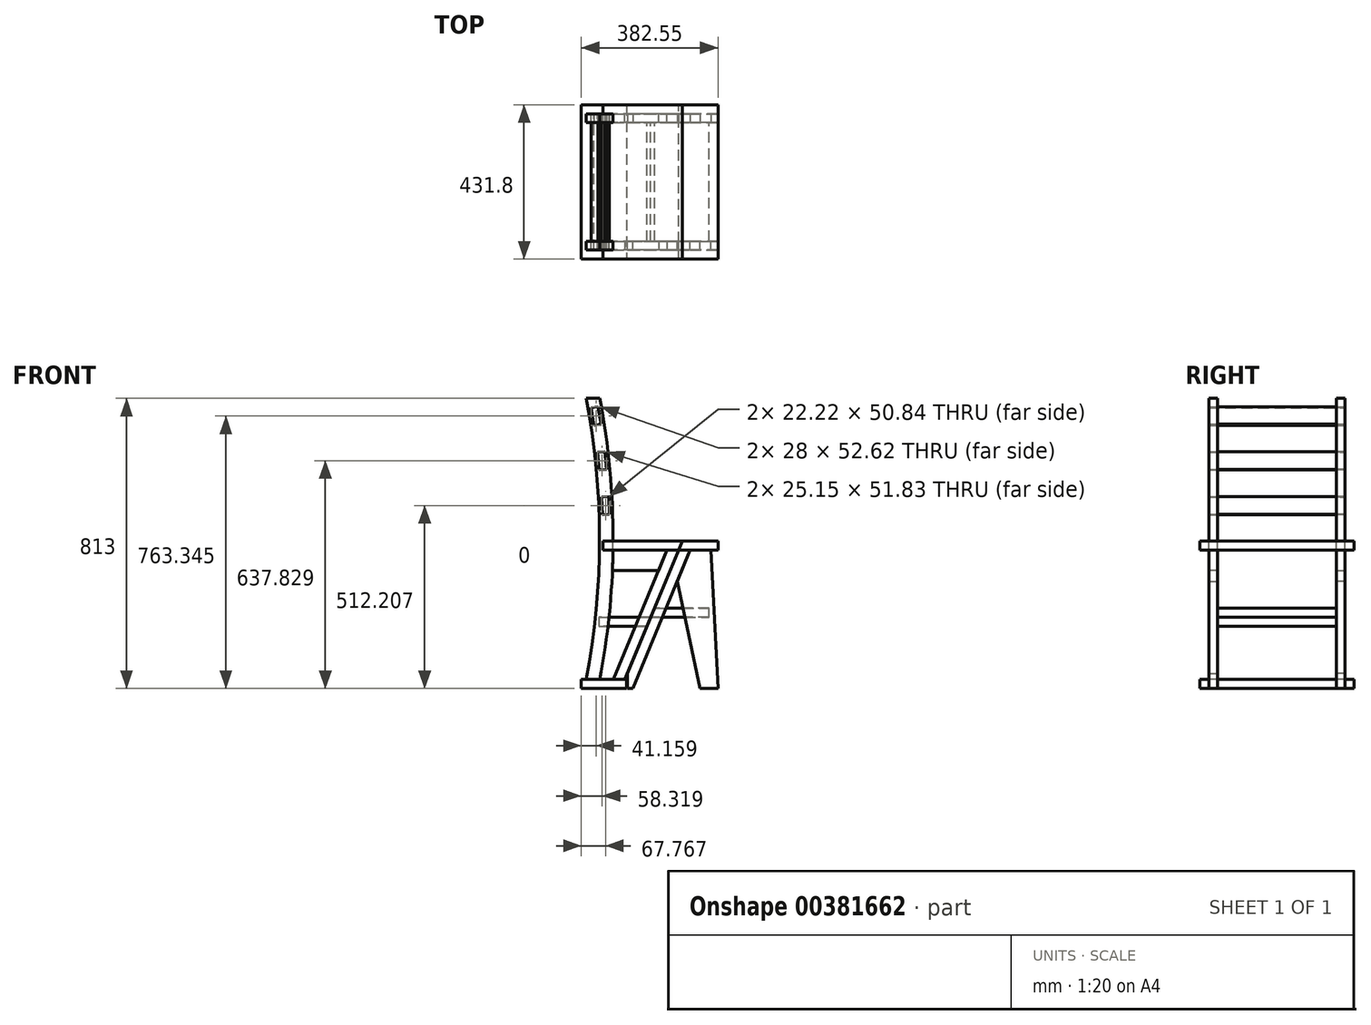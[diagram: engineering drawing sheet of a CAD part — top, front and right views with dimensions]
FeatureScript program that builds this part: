
annotation { "Feature Type Name" : "Feature", "Feature Type Description" : "" }
export const myFeature = defineFeature(function(context is Context, id is Id, definition is map)
    precondition{}
    {
        {
            var Q0;
            Q0=qCreatedBy(makeId("Front.planeOp"),FACE);
            var sketch = newSketch(context, id + "F0", { "sketchPlane" : qUnion([Q0])});
            skLineSegment(sketch, "E0.bottom", {"start": v(0, 25.4) * mm, "end": v(127, 25.4) * mm});
            skLineSegment(sketch, "E0.top", {"start": v(0, 0) * mm, "end": v(127, 0) * mm});
            skLineSegment(sketch, "E0.left", {"start": v(0, 25.4) * mm, "end": v(0, 0) * mm});
            skLineSegment(sketch, "E0.right", {"start": v(127, 25.4) * mm, "end": v(127, 0) * mm});
            skSolve(sketch);
        }
        {
            var Q0;
            Q0 = qSketchRegion(id + "F0", true);
            extrude(context, id + "F1", {"entities" : qUnion([Q0]), "oppositeDirection" : true, "depth" : 431.8 * mm, "offsetDistance" : 25.4 * mm});
        }
        {
            var Q0;
            Q0=makeQuery(id+"F1.opExtrude","SWEPT_EDGE",EDGE,{"disambiguationData":[OSD([sQuery(id+"F0.wireOp",EDGE,"E0.bottom"),sQuery(id+"F0.wireOp",EDGE,"E0.right")])]});
            cPoint(context, id + "F2", {"entities" : qUnion([Q0]), "parameter" : 0.5});
        }
        {
            var Q0;
            Q0=qCreatedBy(makeId("Front.planeOp"),FACE);
            var Q1;
            Q1 = qCreatedBy(id + "F2" ,VERTEX);
            cPlane(context, id + "F3", {"entities" : qUnion([Q0, Q1]), "cplaneType" : CPlaneType.PLANE_POINT, "offset" : 25 * mm, "width" : 150 * mm, "height" : 150 * mm});
        }
        {
            var Q0;
            Q0=makeQuery(id+"F1.opExtrude","CAP_FACE",FACE,{"disambiguationData":[OSD([sQuery(id+"F0.wireOp",EDGE,"E0.bottom"),sQuery(id+"F0.wireOp",EDGE,"E0.top"),sQuery(id+"F0.wireOp",EDGE,"E0.left"),sQuery(id+"F0.wireOp",EDGE,"E0.right")])],"isStart":true});
            cPlane(context, id + "F4", {"entities" : qUnion([Q0]), "cplaneType" : CPlaneType.OFFSET, "offset" : 25 * mm, "oppositeDirection" : true, "width" : 150 * mm, "height" : 150 * mm});
        }
        {
            var Q0;
            Q0=qCreatedBy(id+"F4.planeOp",FACE);
            cPlane(context, id + "F5", {"entities" : qUnion([Q0]), "cplaneType" : CPlaneType.OFFSET, "offset" : 25 * mm, "oppositeDirection" : true, "width" : 150 * mm, "height" : 150 * mm});
        }
        {
            var Q0;
            Q0=qCreatedBy(id+"F3.planeOp",FACE);
            var sketch = newSketch(context, id + "F6", { "sketchPlane" : qUnion([Q0])});
            skLineSegment(sketch, "E1.bottom", {"start": v(49.36, 200) * mm, "end": v(194.32, 200) * mm});
            skLineSegment(sketch, "E1.top", {"start": v(49.36, 175) * mm, "end": v(183.97, 175) * mm});
            skLineSegment(sketch, "E1.left", {"start": v(49.36, 200) * mm, "end": v(49.36, 175) * mm});
            skLineSegment(sketch, "E2", {"start": v(183.97, 175) * mm, "end": v(194.32, 200) * mm});
            skLineSegment(sketch, "E3", {"start": v(183.97, 175) * mm, "end": v(122, 25.4) * mm, "construction": true});
            skLineSegment(sketch, "E4", {"start": v(13, 813) * mm, "end": v(89, 813) * mm, "construction": true});
            skLineSegment(sketch, "E5", {"start": v(13, 25.4) * mm, "end": v(13, 813) * mm, "construction": true});
            skLineSegment(sketch, "E6", {"start": v(89, 813) * mm, "end": v(89, 0) * mm, "construction": true});
            skLineSegment(sketch, "E7", {"start": v(51, 813) * mm, "end": v(51, 0) * mm, "construction": true});
            skArc(sketch, "E8", {"start": v(13, 25.4) * mm, "mid": v(51, 419.2) * mm, "end": v(13, 813) * mm});
            skArc(sketch, "E9.0", {"start": v(51.7, 25.4) * mm, "mid": v(89, 419.2) * mm, "end": v(51.7, 813) * mm});
            skLineSegment(sketch, "E10.bottom", {"start": v(61, 413) * mm, "end": v(282.55, 413) * mm});
            skLineSegment(sketch, "E10.top", {"start": v(61, 388) * mm, "end": v(272.2, 388) * mm});
            skLineSegment(sketch, "E10.left", {"start": v(61, 413) * mm, "end": v(61, 388) * mm});
            skLineSegment(sketch, "E10.right", {"start": v(282.55, 413) * mm, "end": v(272.2, 388) * mm});
            skLineSegment(sketch, "E11.bottom", {"start": v(282.55, 413) * mm, "end": v(382.55, 413) * mm});
            skLineSegment(sketch, "E11.top", {"start": v(272.2, 388) * mm, "end": v(382.55, 388) * mm});
            skLineSegment(sketch, "E11.right", {"start": v(382.55, 413) * mm, "end": v(382.55, 388) * mm});
            skLineSegment(sketch, "E12.bottom", {"start": v(204.68, 225) * mm, "end": v(357.55, 225) * mm});
            skLineSegment(sketch, "E12.top", {"start": v(194.32, 200) * mm, "end": v(357.55, 200) * mm});
            skLineSegment(sketch, "E12.left", {"start": v(204.68, 225) * mm, "end": v(194.32, 200) * mm});
            skLineSegment(sketch, "E12.right", {"start": v(357.55, 225) * mm, "end": v(357.55, 200) * mm});
            skLineSegment(sketch, "E13", {"start": v(13, 813) * mm, "end": v(51.7, 813) * mm});
            skLineSegment(sketch, "E14.0", {"start": v(0, 25.4) * mm, "end": v(127, 25.4) * mm, "construction": true});
            skLineSegment(sketch, "E15", {"start": v(13, 25.4) * mm, "end": v(51.7, 25.4) * mm});
            skLineSegment(sketch, "E16.bottom", {"start": v(27.16, 786.34) * mm, "end": v(46.88, 789.66) * mm});
            skLineSegment(sketch, "E16.top", {"start": v(35.44, 737.03) * mm, "end": v(55.16, 740.35) * mm});
            skLineSegment(sketch, "E16.left", {"start": v(27.16, 786.34) * mm, "end": v(35.44, 737.03) * mm});
            skLineSegment(sketch, "E16.right", {"start": v(46.88, 789.66) * mm, "end": v(55.16, 740.35) * mm});
            skLineSegment(sketch, "E17", {"start": v(45.3, 738.7) * mm, "end": v(37.02, 788) * mm, "construction": true});
            skLineSegment(sketch, "E18", {"start": v(37.02, 788) * mm, "end": v(55.76, 791.15) * mm, "construction": true});
            skLineSegment(sketch, "E19", {"start": v(37.02, 788) * mm, "end": v(18.28, 784.85) * mm, "construction": true});
            skLineSegment(sketch, "E20", {"start": v(45.3, 738.7) * mm, "end": v(64.04, 741.84) * mm, "construction": true});
            skLineSegment(sketch, "E21", {"start": v(45.3, 738.7) * mm, "end": v(26.56, 735.54) * mm, "construction": true});
            skLineSegment(sketch, "E22.bottom", {"start": v(45.74, 661.64) * mm, "end": v(65.63, 663.74) * mm});
            skLineSegment(sketch, "E22.top", {"start": v(51, 611.92) * mm, "end": v(70.9, 614.02) * mm});
            skLineSegment(sketch, "E22.left", {"start": v(45.74, 661.64) * mm, "end": v(51, 611.92) * mm});
            skLineSegment(sketch, "E22.right", {"start": v(65.63, 663.74) * mm, "end": v(70.9, 614.02) * mm});
            skLineSegment(sketch, "E23", {"start": v(60.95, 612.97) * mm, "end": v(55.69, 662.7) * mm, "construction": true});
            skLineSegment(sketch, "E24", {"start": v(55.69, 662.7) * mm, "end": v(74.58, 664.69) * mm, "construction": true});
            skLineSegment(sketch, "E25", {"start": v(55.69, 662.7) * mm, "end": v(36.8, 660.7) * mm, "construction": true});
            skLineSegment(sketch, "E26", {"start": v(60.95, 612.97) * mm, "end": v(79.84, 614.97) * mm, "construction": true});
            skLineSegment(sketch, "E27", {"start": v(60.95, 612.97) * mm, "end": v(42.05, 610.97) * mm, "construction": true});
            skLineSegment(sketch, "E28.bottom", {"start": v(56.66, 536.73) * mm, "end": v(76.64, 537.63) * mm});
            skLineSegment(sketch, "E28.top", {"start": v(58.9, 486.78) * mm, "end": v(78.88, 487.68) * mm});
            skLineSegment(sketch, "E28.left", {"start": v(56.66, 536.73) * mm, "end": v(58.9, 486.78) * mm});
            skLineSegment(sketch, "E28.right", {"start": v(76.64, 537.63) * mm, "end": v(78.88, 487.68) * mm});
            skLineSegment(sketch, "E29", {"start": v(68.89, 487.23) * mm, "end": v(66.65, 537.18) * mm, "construction": true});
            skLineSegment(sketch, "E30", {"start": v(66.65, 537.18) * mm, "end": v(85.63, 538.03) * mm, "construction": true});
            skLineSegment(sketch, "E31", {"start": v(66.65, 537.18) * mm, "end": v(47.67, 536.33) * mm, "construction": true});
            skLineSegment(sketch, "E32", {"start": v(68.89, 487.23) * mm, "end": v(87.87, 488.08) * mm, "construction": true});
            skLineSegment(sketch, "E33", {"start": v(68.89, 487.23) * mm, "end": v(49.9, 486.38) * mm, "construction": true});
            skSolve(sketch);
        }
        {
            var Q0;
            {var subQ12=sQuery(id+"F6.wireOp",EDGE,"E1.left");Q0=makeQuery(id+"F6.imprint","IMPRINT",FACE,{"disambiguationData":[TD([[makeQuery(id+"F6.imprint","IMPRINT",EDGE,{"derivedFrom":subQ12}),-1.0]])]});}
            var Q1;
            {var subQ5=sQuery(id+"F6.wireOp",EDGE,"E10.left");Q1=makeQuery(id+"F6.imprint","IMPRINT",FACE,{"disambiguationData":[TD([[makeQuery(id+"F6.imprint","IMPRINT",EDGE,{"derivedFrom":subQ5}),1.0]])]});}
            var Q2;
            {var subQ3=sQuery(id+"F6.wireOp",EDGE,"E1.left");Q2=makeQuery(id+"F6.imprint","IMPRINT",FACE,{"disambiguationData":[TD([[makeQuery(id+"F6.imprint","IMPRINT",EDGE,{"derivedFrom":subQ3}),1.0]])]});}
            var Q3;
            Q3=qCreatedBy(id+"F4.planeOp",FACE);
            var Q4;
            Q4=qCreatedBy(id+"F5.planeOp",FACE);
            extrude(context, id + "F7", {"entities" : qUnion([Q0, Q1, Q2]), "endBound" : BoundingType.UP_TO_SURFACE, "depth" : 25 * mm, "endBoundEntityFace" : qUnion([Q3]), "offsetDistance" : 25 * mm, "hasSecondDirection" : true, "secondDirectionBound" : SecondDirectionBoundingType.UP_TO_SURFACE, "secondDirectionOppositeDirection" : false, "secondDirectionDepth" : 25 * mm, "secondDirectionBoundEntityFace" : qUnion([Q4])});
        }
        {
            var Q0;
            {var subQ5=sQuery(id+"F6.wireOp",EDGE,"E10.right");Q0=makeQuery(id+"F6.imprint","IMPRINT",FACE,{"disambiguationData":[TD([[makeQuery(id+"F6.imprint","IMPRINT",EDGE,{"derivedFrom":subQ5}),-1.0]])]});}
            var Q1;
            {var subQ5=sQuery(id+"F6.wireOp",EDGE,"E10.left");Q1=makeQuery(id+"F6.imprint","IMPRINT",FACE,{"disambiguationData":[TD([[makeQuery(id+"F6.imprint","IMPRINT",EDGE,{"derivedFrom":subQ5}),1.0]])]});}
            var Q2;
            Q2=makeQuery(id+"F1.opExtrude","CAP_FACE",FACE,{"disambiguationData":[OSD([sQuery(id+"F0.wireOp",EDGE,"E0.bottom"),sQuery(id+"F0.wireOp",EDGE,"E0.top"),sQuery(id+"F0.wireOp",EDGE,"E0.left"),sQuery(id+"F0.wireOp",EDGE,"E0.right")])],"isStart":true});
            var Q3;
            Q3=qCreatedBy(makeId("Origin.pointOp"),VERTEX);
            var Q4;
            Q4=makeQuery(id+"F1.opExtrude","CAP_FACE",FACE,{"disambiguationData":[OSD([sQuery(id+"F0.wireOp",EDGE,"E0.bottom"),sQuery(id+"F0.wireOp",EDGE,"E0.top"),sQuery(id+"F0.wireOp",EDGE,"E0.left"),sQuery(id+"F0.wireOp",EDGE,"E0.right")])],"isStart":false});
            extrude(context, id + "F8", {"entities" : qUnion([Q0, Q1]), "endBound" : BoundingType.UP_TO_SURFACE, "depth" : 25 * mm, "endBoundEntityFace" : qUnion([Q2]), "endBoundEntityVertex" : qUnion([Q3]), "offsetDistance" : 25 * mm, "hasSecondDirection" : true, "secondDirectionBound" : SecondDirectionBoundingType.UP_TO_SURFACE, "secondDirectionOppositeDirection" : true, "secondDirectionDepth" : 25 * mm, "secondDirectionBoundEntityFace" : qUnion([Q4])});
        }
        {
            var Q0;
            Q0=qCreatedBy(id+"F4.planeOp",FACE);
            var sketch = newSketch(context, id + "F9", { "sketchPlane" : qUnion([Q0])});
            skLineSegment(sketch, "E34", {"start": v(272.2, 388) * mm, "end": v(122, 25.4) * mm});
            skLineSegment(sketch, "E35", {"start": v(239.72, 388) * mm, "end": v(89.53, 25.4) * mm});
            skLineSegment(sketch, "E36", {"start": v(239.72, 388) * mm, "end": v(272.2, 388) * mm});
            skLineSegment(sketch, "E37", {"start": v(89.53, 25.4) * mm, "end": v(122, 25.4) * mm});
            skSolve(sketch);
        }
        {
            var Q0;
            Q0=makeQuery(id+"F9.imprint","IMPRINT",FACE,{"disambiguationData":[TD([[makeQuery(id+"F9.imprint","IMPRINT",EDGE,{"derivedFrom":sQuery(id+"F9.wireOp",EDGE,"E34")}),-1.0]])]});
            extrude(context, id + "F10", {"entities" : qUnion([Q0]), "oppositeDirection" : true, "depth" : 25 * mm, "offsetDistance" : 25 * mm});
        }
        {
            var Q0;
            Q0=qCreatedBy(id+"F4.planeOp",FACE);
            var sketch = newSketch(context, id + "F11", { "sketchPlane" : qUnion([Q0])});
            skLineSegment(sketch, "E38", {"start": v(87.14, 331) * mm, "end": v(216.11, 331) * mm});
            skLineSegment(sketch, "E39.0", {"start": v(239.72, 388) * mm, "end": v(216.11, 331) * mm});
            skLineSegment(sketch, "E40.0", {"start": v(88.77, 388) * mm, "end": v(239.72, 388) * mm});
            skArc(sketch, "E41.0", {"start": v(87.14, 331) * mm, "mid": v(88.15, 359.5) * mm, "end": v(88.77, 388) * mm});
            skSolve(sketch);
        }
        {
            var Q0;
            Q0=makeQuery(id+"F11.imprint","IMPRINT",FACE,{"disambiguationData":[TD([[makeQuery(id+"F11.imprint","IMPRINT",EDGE,{"derivedFrom":sQuery(id+"F11.wireOp",EDGE,"E38")}),1.0]])]});
            extrude(context, id + "F12", {"entities" : qUnion([Q0]), "oppositeDirection" : true, "depth" : 25 * mm, "offsetDistance" : 25 * mm});
        }
        {
            var Q0;
            Q0=makeQuery(id+"F12.opExtrude","SWEPT_BODY",BODY,{"disambiguationData":[OSD([sQuery(id+"F11.wireOp",EDGE,"E38"),sQuery(id+"F11.wireOp",EDGE,"E39.0"),sQuery(id+"F11.wireOp",EDGE,"4ce61eea-0b09-489c-b5a4-3acdd70acc47.0"),sQuery(id+"F11.wireOp",EDGE,"E40.0")])]});
            var Q1;
            Q1=makeQuery(id+"F10.opExtrude","SWEPT_BODY",BODY,{"disambiguationData":[OSD([sQuery(id+"F9.wireOp",EDGE,"E34"),sQuery(id+"F9.wireOp",EDGE,"E35"),sQuery(id+"F9.wireOp",EDGE,"E36"),sQuery(id+"F9.wireOp",EDGE,"E37")])]});
            var Q2;
            Q2=makeQuery(id+"F7.opExtrude","SWEPT_BODY",BODY,{"disambiguationData":[OSD([sQuery(id+"F6.wireOp",EDGE,"E8"),sQuery(id+"F6.wireOp",EDGE,"E9.0"),sQuery(id+"F6.wireOp",EDGE,"E13"),sQuery(id+"F6.wireOp",EDGE,"nrl6pul6-bRE5-QjhI-z4ZE-iPqJKix11UCx")])]});
            var Q3;
            Q3=qCreatedBy(id+"F3.planeOp",FACE);
            mirror(context, id + "F13", {"entities" : qUnion([Q0, Q1, Q2]), "mirrorPlane" : qUnion([Q3])});
        }
        {
            var Q0;
            {var subQ3=sQuery(id+"F6.wireOp",EDGE,"E2");Q0=makeQuery(id+"F6.imprint","IMPRINT",FACE,{"disambiguationData":[TD([[makeQuery(id+"F6.imprint","IMPRINT",EDGE,{"derivedFrom":subQ3}),1.0]])]});}
            var Q1;
            {var subQ3=sQuery(id+"F6.wireOp",EDGE,"E1.left");Q1=makeQuery(id+"F6.imprint","IMPRINT",FACE,{"disambiguationData":[TD([[makeQuery(id+"F6.imprint","IMPRINT",EDGE,{"derivedFrom":subQ3}),1.0]])]});}
            var Q2;
            Q2=makeQuery(id+"F7.opExtrude","CAP_FACE",FACE,{"disambiguationData":[OSD([sQuery(id+"F6.wireOp",EDGE,"E8"),sQuery(id+"F6.wireOp",EDGE,"E9.0"),sQuery(id+"F6.wireOp",EDGE,"E13"),sQuery(id+"F6.wireOp",EDGE,"nrl6pul6-bRE5-QjhI-z4ZE-iPqJKix11UCx")])],"isStart":true});
            var Q3;
            Q3=makeQuery(id+"F13.opPattern","COPY",FACE,{"derivedFrom":makeQuery(id+"F7.opExtrude","CAP_FACE",FACE,{"disambiguationData":[OSD([sQuery(id+"F6.wireOp",EDGE,"E8"),sQuery(id+"F6.wireOp",EDGE,"E9.0"),sQuery(id+"F6.wireOp",EDGE,"E13"),sQuery(id+"F6.wireOp",EDGE,"nrl6pul6-bRE5-QjhI-z4ZE-iPqJKix11UCx")])],"isStart":true}),"instanceName":"1"});
            extrude(context, id + "F14", {"entities" : qUnion([Q0, Q1]), "endBound" : BoundingType.UP_TO_SURFACE, "depth" : 25 * mm, "endBoundEntityFace" : qUnion([Q2]), "offsetDistance" : 25 * mm, "hasSecondDirection" : true, "secondDirectionBound" : SecondDirectionBoundingType.UP_TO_SURFACE, "secondDirectionOppositeDirection" : true, "secondDirectionDepth" : 25 * mm, "secondDirectionBoundEntityFace" : qUnion([Q3])});
        }
        {
            var Q0;
            Q0=makeQuery(id+"F6.imprint","IMPRINT",FACE,{"disambiguationData":[TD([[makeQuery(id+"F6.imprint","IMPRINT",EDGE,{"derivedFrom":sQuery(id+"F6.wireOp",EDGE,"E16.bottom")}),-1.0]])]});
            var Q1;
            Q1=makeQuery(id+"F6.imprint","IMPRINT",FACE,{"disambiguationData":[TD([[makeQuery(id+"F6.imprint","IMPRINT",EDGE,{"derivedFrom":sQuery(id+"F6.wireOp",EDGE,"E22.bottom")}),-1.0]])]});
            var Q2;
            Q2=makeQuery(id+"F6.imprint","IMPRINT",FACE,{"disambiguationData":[TD([[makeQuery(id+"F6.imprint","IMPRINT",EDGE,{"derivedFrom":sQuery(id+"F6.wireOp",EDGE,"E28.bottom")}),-1.0]])]});
            var Q3;
            Q3=makeQuery(id+"F7.opExtrude","CAP_FACE",FACE,{"disambiguationData":[OSD([sQuery(id+"F6.wireOp",EDGE,"E8"),sQuery(id+"F6.wireOp",EDGE,"E9.0"),sQuery(id+"F6.wireOp",EDGE,"E13"),sQuery(id+"F6.wireOp",EDGE,"E15"),sQuery(id+"F6.wireOp",EDGE,"E16.bottom"),sQuery(id+"F6.wireOp",EDGE,"E16.top"),sQuery(id+"F6.wireOp",EDGE,"E16.left"),sQuery(id+"F6.wireOp",EDGE,"E16.right"),sQuery(id+"F6.wireOp",EDGE,"E22.bottom"),sQuery(id+"F6.wireOp",EDGE,"E22.top"),sQuery(id+"F6.wireOp",EDGE,"E22.left"),sQuery(id+"F6.wireOp",EDGE,"E22.right"),sQuery(id+"F6.wireOp",EDGE,"E28.bottom"),sQuery(id+"F6.wireOp",EDGE,"E28.top"),sQuery(id+"F6.wireOp",EDGE,"E28.left"),sQuery(id+"F6.wireOp",EDGE,"E28.right")])],"isStart":false});
            var Q4;
            Q4=makeQuery(id+"F13.opPattern","COPY",FACE,{"derivedFrom":makeQuery(id+"F7.opExtrude","CAP_FACE",FACE,{"disambiguationData":[OSD([sQuery(id+"F6.wireOp",EDGE,"E8"),sQuery(id+"F6.wireOp",EDGE,"E9.0"),sQuery(id+"F6.wireOp",EDGE,"E13"),sQuery(id+"F6.wireOp",EDGE,"E15"),sQuery(id+"F6.wireOp",EDGE,"E16.bottom"),sQuery(id+"F6.wireOp",EDGE,"E16.top"),sQuery(id+"F6.wireOp",EDGE,"E16.left"),sQuery(id+"F6.wireOp",EDGE,"E16.right"),sQuery(id+"F6.wireOp",EDGE,"E22.bottom"),sQuery(id+"F6.wireOp",EDGE,"E22.top"),sQuery(id+"F6.wireOp",EDGE,"E22.left"),sQuery(id+"F6.wireOp",EDGE,"E22.right"),sQuery(id+"F6.wireOp",EDGE,"E28.bottom"),sQuery(id+"F6.wireOp",EDGE,"E28.top"),sQuery(id+"F6.wireOp",EDGE,"E28.left"),sQuery(id+"F6.wireOp",EDGE,"E28.right")])],"isStart":false}),"instanceName":"1"});
            extrude(context, id + "F15", {"entities" : qUnion([Q0, Q1, Q2]), "endBound" : BoundingType.UP_TO_SURFACE, "depth" : 25 * mm, "endBoundEntityFace" : qUnion([Q3]), "offsetDistance" : 25 * mm, "hasSecondDirection" : true, "secondDirectionBound" : SecondDirectionBoundingType.UP_TO_SURFACE, "secondDirectionOppositeDirection" : true, "secondDirectionDepth" : 25 * mm, "secondDirectionBoundEntityFace" : qUnion([Q4])});
        }
        {
            var Q0;
            Q0=makeQuery(id+"F6.imprint","IMPRINT",FACE,{"disambiguationData":[TD([[makeQuery(id+"F6.imprint","IMPRINT",EDGE,{"derivedFrom":sQuery(id+"F6.wireOp",EDGE,"E10.right")}),1.0]])]});
            var Q1;
            Q1=makeQuery(id+"F8.opExtrude","CAP_FACE",FACE,{"disambiguationData":[OSD([sQuery(id+"F6.wireOp",EDGE,"E10.bottom"),sQuery(id+"F6.wireOp",EDGE,"E10.top"),sQuery(id+"F6.wireOp",EDGE,"E10.left"),sQuery(id+"F6.wireOp",EDGE,"E10.right")])],"isStart":false});
            var Q2;
            Q2=makeQuery(id+"F8.opExtrude","CAP_FACE",FACE,{"disambiguationData":[OSD([sQuery(id+"F6.wireOp",EDGE,"E10.bottom"),sQuery(id+"F6.wireOp",EDGE,"E10.top"),sQuery(id+"F6.wireOp",EDGE,"E10.left"),sQuery(id+"F6.wireOp",EDGE,"E10.right")])],"isStart":true});
            extrude(context, id + "F16", {"entities" : qUnion([Q0]), "endBound" : BoundingType.UP_TO_SURFACE, "depth" : 25 * mm, "endBoundEntityFace" : qUnion([Q1]), "offsetDistance" : 25 * mm, "hasSecondDirection" : true, "secondDirectionBound" : SecondDirectionBoundingType.UP_TO_SURFACE, "secondDirectionOppositeDirection" : true, "secondDirectionDepth" : 25 * mm, "secondDirectionBoundEntityFace" : qUnion([Q2])});
        }
        {
            var Q0;
            Q0=makeQuery(id+"F6.imprint","IMPRINT",FACE,{"disambiguationData":[TD([[makeQuery(id+"F6.imprint","IMPRINT",EDGE,{"derivedFrom":sQuery(id+"F6.wireOp",EDGE,"E12.bottom")}),-1.0]])]});
            var Q1;
            Q1=makeQuery(id+"F10.opExtrude","CAP_FACE",FACE,{"disambiguationData":[OSD([sQuery(id+"F9.wireOp",EDGE,"E34"),sQuery(id+"F9.wireOp",EDGE,"E35"),sQuery(id+"F9.wireOp",EDGE,"E36"),sQuery(id+"F9.wireOp",EDGE,"E37")])],"isStart":false});
            var Q2;
            Q2=makeQuery(id+"F13.opPattern","COPY",FACE,{"derivedFrom":makeQuery(id+"F10.opExtrude","CAP_FACE",FACE,{"disambiguationData":[OSD([sQuery(id+"F9.wireOp",EDGE,"E34"),sQuery(id+"F9.wireOp",EDGE,"E35"),sQuery(id+"F9.wireOp",EDGE,"E36"),sQuery(id+"F9.wireOp",EDGE,"E37")])],"isStart":false}),"instanceName":"1"});
            extrude(context, id + "F17", {"entities" : qUnion([Q0]), "endBound" : BoundingType.UP_TO_SURFACE, "depth" : 25 * mm, "endBoundEntityFace" : qUnion([Q1]), "offsetDistance" : 25 * mm, "hasSecondDirection" : true, "secondDirectionBound" : SecondDirectionBoundingType.UP_TO_SURFACE, "secondDirectionOppositeDirection" : true, "secondDirectionDepth" : 25 * mm, "secondDirectionBoundEntityFace" : qUnion([Q2])});
        }
        {
            var Q0;
            Q0=qCreatedBy(id+"F3.planeOp",FACE);
            var sketch = newSketch(context, id + "F18", { "sketchPlane" : qUnion([Q0])});
            skLineSegment(sketch, "E42", {"start": v(129, 42.3) * mm, "end": v(272.2, 388) * mm});
            skLineSegment(sketch, "E43", {"start": v(272.2, 388) * mm, "end": v(304.67, 388) * mm});
            skLineSegment(sketch, "E44", {"start": v(129, 0) * mm, "end": v(143.95, 0) * mm});
            skLineSegment(sketch, "E45", {"start": v(304.67, 388) * mm, "end": v(143.95, 0) * mm});
            skLineSegment(sketch, "E46", {"start": v(129, 0) * mm, "end": v(129, 42.3) * mm});
            skSolve(sketch);
        }
        {
            var Q0;
            Q0 = qSketchRegion(id + "F18", true);
            var Q1;
            Q1=makeQuery(id+"F10.opExtrude","CAP_FACE",FACE,{"disambiguationData":[OSD([sQuery(id+"F9.wireOp",EDGE,"E34"),sQuery(id+"F9.wireOp",EDGE,"E35"),sQuery(id+"F9.wireOp",EDGE,"E36"),sQuery(id+"F9.wireOp",EDGE,"E37")])],"isStart":true});
            var Q2;
            Q2=makeQuery(id+"F10.opExtrude","CAP_FACE",FACE,{"disambiguationData":[OSD([sQuery(id+"F9.wireOp",EDGE,"E34"),sQuery(id+"F9.wireOp",EDGE,"E35"),sQuery(id+"F9.wireOp",EDGE,"E36"),sQuery(id+"F9.wireOp",EDGE,"E37")])],"isStart":false});
            extrude(context, id + "F19", {"entities" : qUnion([Q0]), "endBound" : BoundingType.UP_TO_SURFACE, "depth" : 25 * mm, "endBoundEntityFace" : qUnion([Q1]), "offsetDistance" : 25 * mm, "hasSecondDirection" : true, "secondDirectionBound" : SecondDirectionBoundingType.UP_TO_SURFACE, "secondDirectionOppositeDirection" : false, "secondDirectionDepth" : 25 * mm, "secondDirectionBoundEntityFace" : qUnion([Q2])});
        }
        {
            var Q0;
            Q0=makeQuery(id+"F19.opExtrude","SWEPT_BODY",BODY,{"disambiguationData":[OSD([sQuery(id+"F18.wireOp",EDGE,"E42"),sQuery(id+"F18.wireOp",EDGE,"E43"),sQuery(id+"F18.wireOp",EDGE,"E44"),sQuery(id+"F18.wireOp",EDGE,"E45"),sQuery(id+"F18.wireOp",EDGE,"E46")])]});
            var Q1;
            Q1=qCreatedBy(id+"F3.planeOp",FACE);
            mirror(context, id + "F20", {"entities" : qUnion([Q0]), "mirrorPlane" : qUnion([Q1])});
        }
        {
            var Q0;
            Q0=qCreatedBy(id+"F3.planeOp",FACE);
            var sketch = newSketch(context, id + "F21", { "sketchPlane" : qUnion([Q0])});
            skLineSegment(sketch, "E47", {"start": v(362.55, 388) * mm, "end": v(382.55, 0) * mm});
            skLineSegment(sketch, "E48", {"start": v(382.55, 0) * mm, "end": v(332.55, 0) * mm});
            skLineSegment(sketch, "E49", {"start": v(332.55, 0) * mm, "end": v(268.21, 300) * mm});
            skLineSegment(sketch, "E50", {"start": v(268.21, 300) * mm, "end": v(304.67, 388) * mm});
            skLineSegment(sketch, "E51", {"start": v(304.67, 388) * mm, "end": v(362.55, 388) * mm});
            skSolve(sketch);
        }
        {
            var Q0;
            Q0=makeQuery(id+"F21.imprint","IMPRINT",FACE,{"disambiguationData":[TD([[makeQuery(id+"F21.imprint","IMPRINT",EDGE,{"derivedFrom":sQuery(id+"F21.wireOp",EDGE,"E47")}),-1.0]])]});
            var Q1;
            Q1=makeQuery(id+"F19.opExtrude","CAP_FACE",FACE,{"disambiguationData":[OSD([sQuery(id+"F18.wireOp",EDGE,"E42"),sQuery(id+"F18.wireOp",EDGE,"E43"),sQuery(id+"F18.wireOp",EDGE,"E44"),sQuery(id+"F18.wireOp",EDGE,"E45"),sQuery(id+"F18.wireOp",EDGE,"E46")])],"isStart":false});
            var Q2;
            Q2=makeQuery(id+"F19.opExtrude","CAP_FACE",FACE,{"disambiguationData":[OSD([sQuery(id+"F18.wireOp",EDGE,"E42"),sQuery(id+"F18.wireOp",EDGE,"E43"),sQuery(id+"F18.wireOp",EDGE,"E44"),sQuery(id+"F18.wireOp",EDGE,"E45"),sQuery(id+"F18.wireOp",EDGE,"E46")])],"isStart":true});
            extrude(context, id + "F22", {"entities" : qUnion([Q0]), "endBound" : BoundingType.UP_TO_SURFACE, "depth" : 25 * mm, "endBoundEntityFace" : qUnion([Q1]), "offsetDistance" : 25 * mm, "hasSecondDirection" : true, "secondDirectionBound" : SecondDirectionBoundingType.UP_TO_SURFACE, "secondDirectionOppositeDirection" : false, "secondDirectionDepth" : 25 * mm, "secondDirectionBoundEntityFace" : qUnion([Q2])});
        }
        {
            var Q0;
            Q0=makeQuery(id+"F22.opExtrude","SWEPT_BODY",BODY,{"disambiguationData":[OSD([sQuery(id+"F21.wireOp",EDGE,"E47"),sQuery(id+"F21.wireOp",EDGE,"E48"),sQuery(id+"F21.wireOp",EDGE,"E49"),sQuery(id+"F21.wireOp",EDGE,"E50"),sQuery(id+"F21.wireOp",EDGE,"E51")])]});
            var Q1;
            Q1=qCreatedBy(id+"F3.planeOp",FACE);
            mirror(context, id + "F23", {"entities" : qUnion([Q0]), "mirrorPlane" : qUnion([Q1])});
        }
    });
